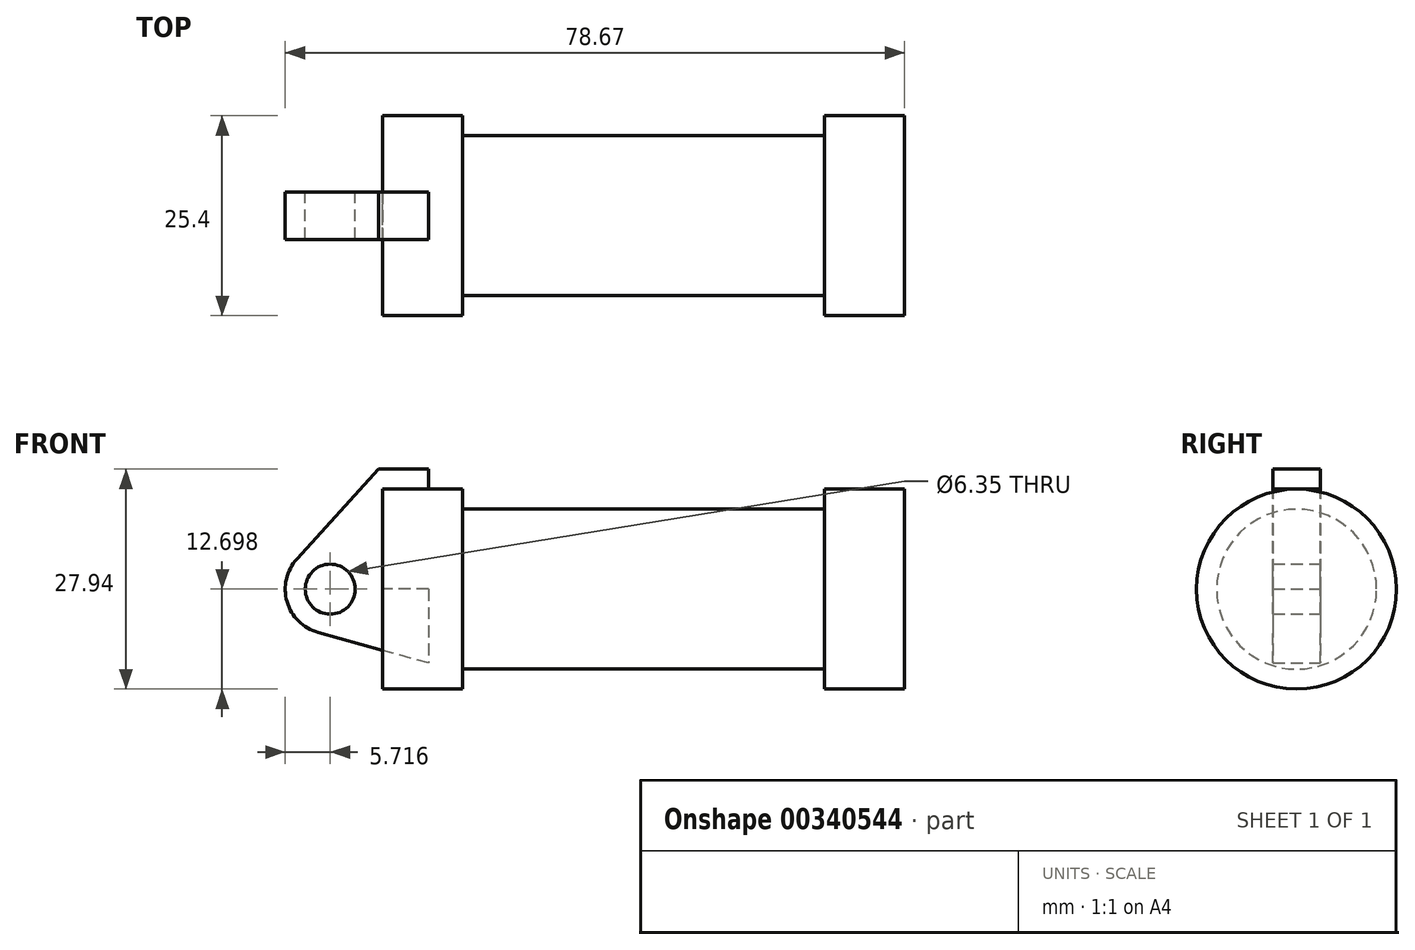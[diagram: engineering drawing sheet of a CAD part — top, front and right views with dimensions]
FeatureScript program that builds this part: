
annotation { "Feature Type Name" : "Feature", "Feature Type Description" : "" }
export const myFeature = defineFeature(function(context is Context, id is Id, definition is map)
    precondition{}
    {
        {
            var Q0;
            Q0=qCreatedBy(makeId("Front.planeOp"),FACE);
            var sketch = newSketch(context, id + "F0", { "sketchPlane" : qUnion([Q0])});
            skLineSegment(sketch, "E0", {"start": v(-16.68, -6.1) * mm, "end": v(-16.68, 6.6) * mm});
            skLineSegment(sketch, "E1", {"start": v(-16.68, 6.6) * mm, "end": v(-6.52, 6.6) * mm});
            skLineSegment(sketch, "E2", {"start": v(-6.52, 6.6) * mm, "end": v(-6.52, 4.07) * mm});
            skLineSegment(sketch, "E3", {"start": v(-6.52, 4.07) * mm, "end": v(39.46, 4.07) * mm});
            skLineSegment(sketch, "E4", {"start": v(39.46, 4.07) * mm, "end": v(39.46, 6.6) * mm});
            skLineSegment(sketch, "E5", {"start": v(39.46, 6.6) * mm, "end": v(49.62, 6.6) * mm});
            skLineSegment(sketch, "E6", {"start": v(49.62, 6.6) * mm, "end": v(49.62, -6.1) * mm});
            skLineSegment(sketch, "E7", {"start": v(49.62, -6.1) * mm, "end": v(-16.68, -6.1) * mm});
            skLineSegment(sketch, "E8", {"start": v(-10.84, 9.15) * mm, "end": v(-17.19, 9.15) * mm});
            skLineSegment(sketch, "E9", {"start": v(-17.19, 9.15) * mm, "end": v(-27.56, -2.24) * mm});
            skLineSegment(sketch, "E10", {"start": v(-16.68, -6.1) * mm, "end": v(-23.33, -6.1) * mm});
            skCircle(sketch, "E11", {"center": v(-23.33, -6.1) * mm, "radius": 5.72 * mm});
            skCircle(sketch, "E12", {"center": v(-23.33, -6.1) * mm, "radius": 3.18 * mm});
            skLineSegment(sketch, "E13", {"start": v(-10.84, 9.15) * mm, "end": v(-10.84, -15.49) * mm});
            skLineSegment(sketch, "E14", {"start": v(-10.84, -15.49) * mm, "end": v(-24.86, -11.6) * mm});
            skSolve(sketch);
        }
        {
            var Q0;
            {var subQ0=sQuery(id+"F0.wireOp",EDGE,"E2");Q0=makeQuery(id+"F0.imprint","IMPRINT",FACE,{"disambiguationData":[TD([[makeQuery(id+"F0.imprint","IMPRINT",EDGE,{"derivedFrom":subQ0}),-1.0]])]});}
            var Q1;
            {var subQ0=sQuery(id+"F0.wireOp",EDGE,"E0");Q1=makeQuery(id+"F0.imprint","IMPRINT",FACE,{"disambiguationData":[TD([[makeQuery(id+"F0.imprint","IMPRINT",EDGE,{"derivedFrom":subQ0}),-1.0]])]});}
            var Q2;
            Q2=sQuery(id+"F0.wireOp",EDGE,"E7");
            revolve(context, id + "F1", {"entities" : qUnion([Q0, Q1]), "axis" : qUnion([Q2]), "revolveType" : RevolveType.FULL});
        }
        {
            var Q0;
            Q0=makeQuery(id+"F0.imprint","IMPRINT",FACE,{"disambiguationData":[TD([[makeQuery(id+"F0.imprint","IMPRINT",EDGE,{"derivedFrom":sQuery(id+"F0.wireOp",EDGE,"E12")}),-1.0]])]});
            var Q1;
            {var subQ1=sQuery(id+"F0.wireOp",EDGE,"E0");Q1=makeQuery(id+"F0.imprint","IMPRINT",FACE,{"disambiguationData":[TD([[makeQuery(id+"F0.imprint","IMPRINT",EDGE,{"derivedFrom":subQ1}),1.0]])]});}
            var Q2;
            {var subQ0=sQuery(id+"F0.wireOp",EDGE,"E14");Q2=makeQuery(id+"F0.imprint","IMPRINT",FACE,{"disambiguationData":[TD([[makeQuery(id+"F0.imprint","IMPRINT",EDGE,{"derivedFrom":subQ0}),-1.0]])]});}
            extrude(context, id + "F2", {"entities" : qUnion([Q0, Q1, Q2]), "endBound" : BoundingType.SYMMETRIC, "depth" : 6 * mm});
        }
    });
